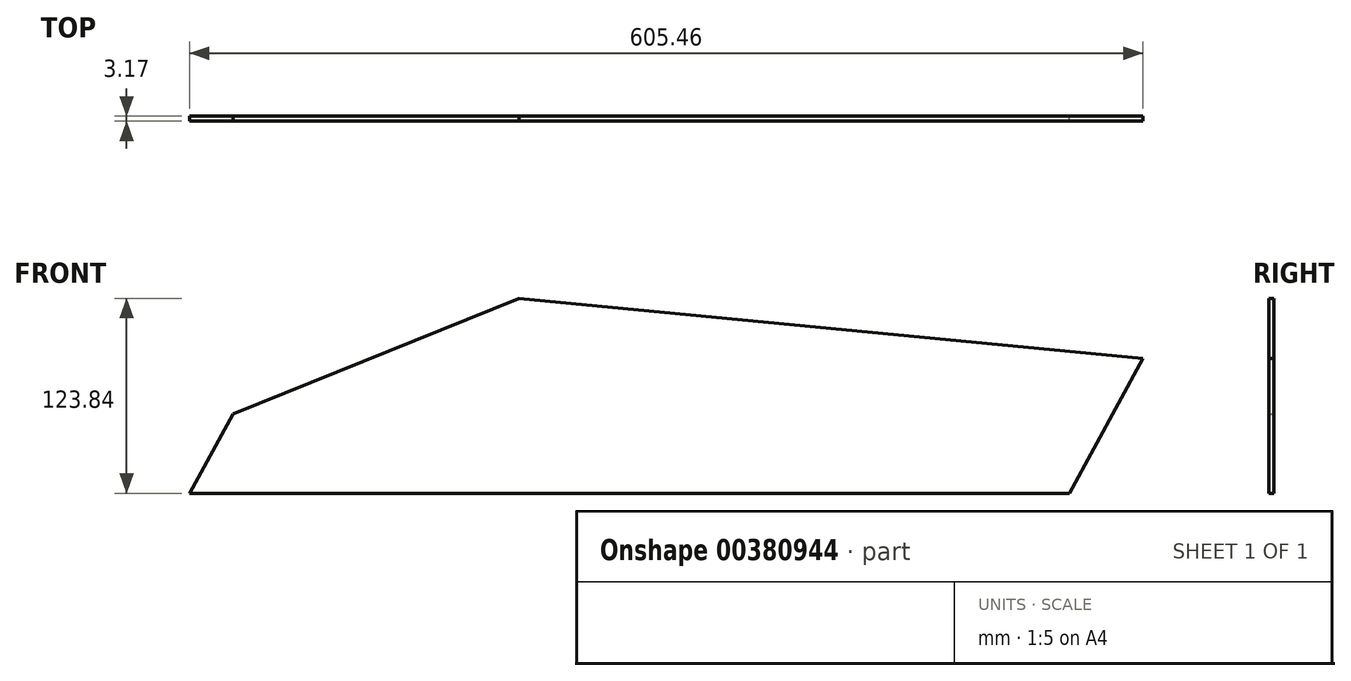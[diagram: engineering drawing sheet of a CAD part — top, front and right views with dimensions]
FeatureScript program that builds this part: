
annotation { "Feature Type Name" : "Feature", "Feature Type Description" : "" }
export const myFeature = defineFeature(function(context is Context, id is Id, definition is map)
    precondition{}
    {
        {
            var Q0;
            Q0=qCreatedBy(makeId("Front.planeOp"),FACE);
            var sketch = newSketch(context, id + "F0", { "sketchPlane" : qUnion([Q0])});
            skLineSegment(sketch, "E0", {"start": v(0, 0) * mm, "end": v(-558.8, 0) * mm});
            skLineSegment(sketch, "E1", {"start": v(-558.8, 0) * mm, "end": v(-531.34, 50.4) * mm});
            skLineSegment(sketch, "E2", {"start": v(-531.34, 50.4) * mm, "end": v(-349.52, 123.84) * mm});
            skLineSegment(sketch, "E3", {"start": v(-349.52, 123.84) * mm, "end": v(46.66, 85.65) * mm});
            skLineSegment(sketch, "E4", {"start": v(46.66, 85.65) * mm, "end": v(0, 0) * mm});
            skSolve(sketch);
        }
        {
            var Q0;
            Q0 = qSketchRegion(id + "F0", true);
            extrude(context, id + "F1", {"entities" : qUnion([Q0]), "depth" : 3.17 * mm});
        }
    });
